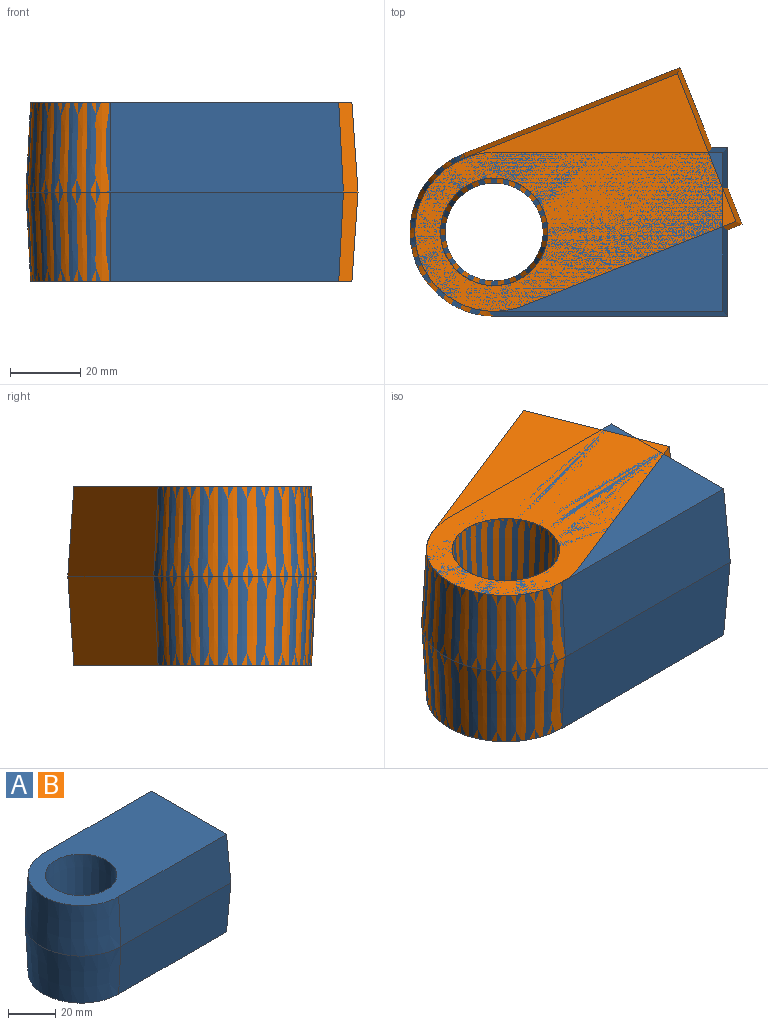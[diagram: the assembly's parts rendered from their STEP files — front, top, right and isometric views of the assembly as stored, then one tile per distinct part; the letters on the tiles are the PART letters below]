
ASSEMBLY  parts=2 mates=1
PART A: 12 faces, bbox 90.1x47.8x50.8 mm
  f0: plane 66.2x25.4mm, normal (0,1,0.05), area 1666.7mm2, adj f1,f3,f5,f9
  f1: cone r=23.89mm half-angle=3deg, axis (0,0,-1), area 1855.6mm2, adj f0,f2,f5,f8
  f2: plane 66.2x25.4mm, normal (0,-1,0.05), area 1666.7mm2, adj f1,f3,f5,f7
  f3: plane 47.78x25.4mm, normal (1,0,0.05), area 1181.3mm2, adj f0,f2,f5,f6
  f4: cone r=13.92mm half-angle=3deg, axis (0,0,1), area 2331.3mm2, adj f5,f11
  f5: plane 87.42x45.11mm, normal (0,0,1), area 2994.5mm2, adj f0,f1,f2,f3,f4
  f6: plane 47.78x25.4mm, normal (1,0,-0.05), area 1181.3mm2, adj f3,f7,f9,f10
  f7: plane 66.2x25.4mm, normal (0,-1,-0.05), area 1666.7mm2, adj f2,f6,f8,f10
  f8: cone r=23.89mm half-angle=3deg, axis (0,0,1), area 1855.6mm2, adj f1,f7,f9,f10
  f9: plane 66.2x25.4mm, normal (0,1,-0.05), area 1666.7mm2, adj f0,f6,f8,f10
  f10: plane 87.42x45.11mm, normal (0,0,-1), area 2994.5mm2, adj f6,f7,f8,f9,f11
  f11: cone r=13.92mm half-angle=3deg, axis (0,0,-1), area 2331.3mm2, adj f4,f10
PART B: same geometry as A
PLACE A t=(-8.29,-9.02,8.39)mm fixed
PLACE B rot(axis=(0,0,1),21.6deg) t=(-11.05,5.13,8.39)mm
MATE revolute A.f1 <-> B.f1  axis (0,0,1) through (-46.72,-9.16,33.79)mm
